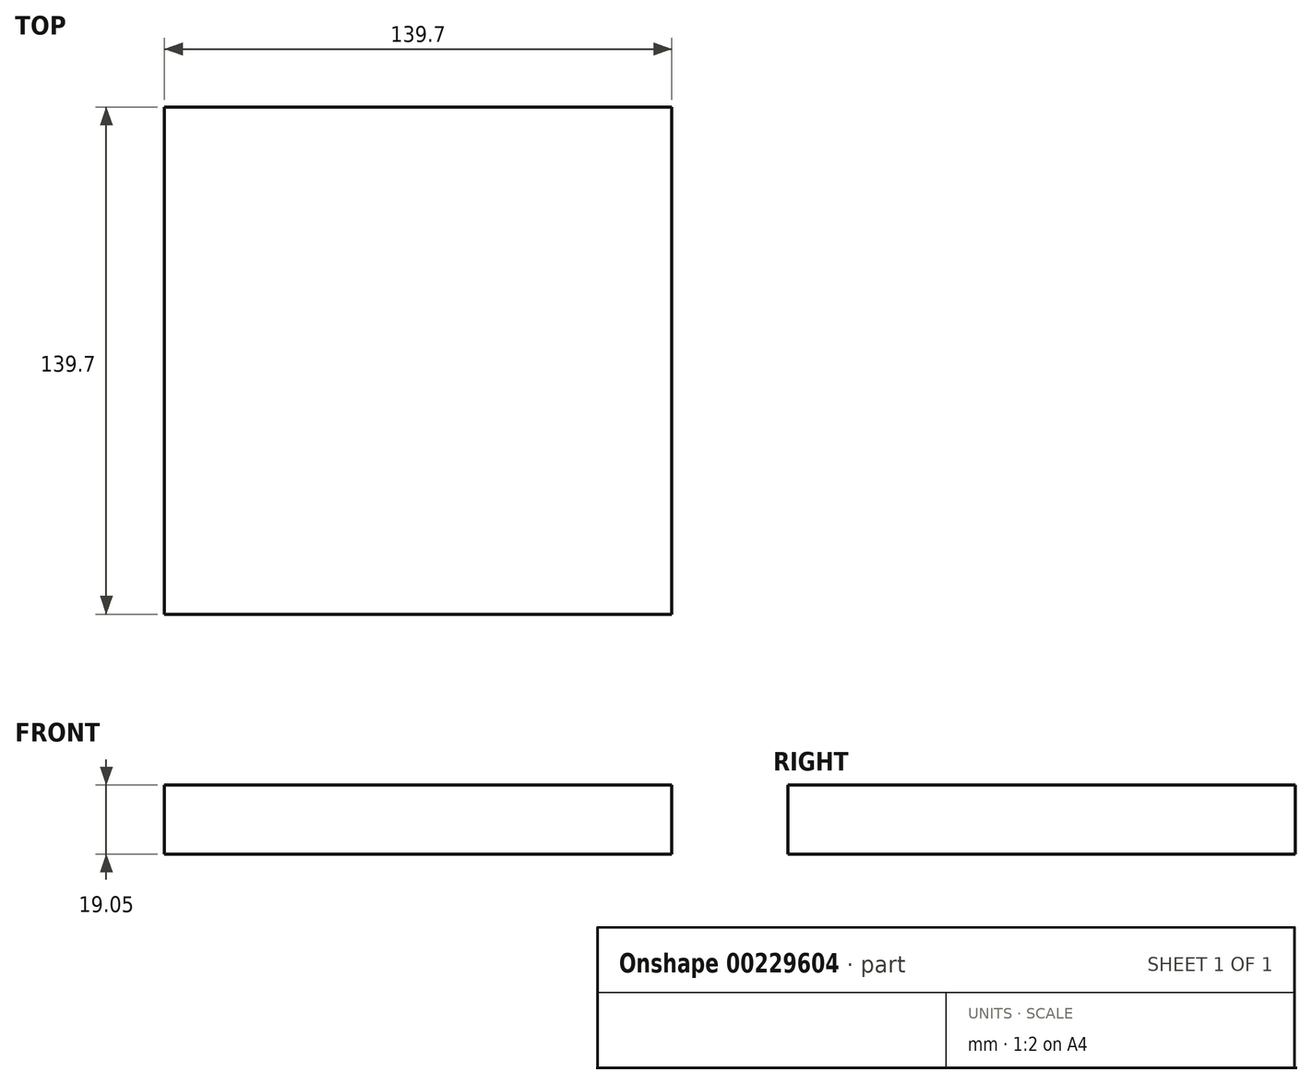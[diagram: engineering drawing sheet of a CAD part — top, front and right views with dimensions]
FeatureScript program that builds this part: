
annotation { "Feature Type Name" : "Feature", "Feature Type Description" : "" }
export const myFeature = defineFeature(function(context is Context, id is Id, definition is map)
    precondition{}
    {
        {
            var Q0;
            Q0=qCreatedBy(makeId("Top.planeOp"),FACE);
            var sketch = newSketch(context, id + "F0", { "sketchPlane" : qUnion([Q0])});
            skLineSegment(sketch, "E0.bottom", {"start": v(69.85, -69.85) * mm, "end": v(-69.85, -69.85) * mm});
            skLineSegment(sketch, "E0.top", {"start": v(69.85, 69.85) * mm, "end": v(-69.85, 69.85) * mm});
            skLineSegment(sketch, "E0.left", {"start": v(69.85, -69.85) * mm, "end": v(69.85, 69.85) * mm});
            skLineSegment(sketch, "E0.right", {"start": v(-69.85, -69.85) * mm, "end": v(-69.85, 69.85) * mm});
            skPoint(sketch, "E0.middle", {"position": v(0, 0) * mm});
            skSolve(sketch);
        }
        {
            var Q0;
            Q0 = qSketchRegion(id + "F0", true);
            extrude(context, id + "F1", {"entities" : qUnion([Q0]), "depth" : 19.05 * mm});
        }
    });
